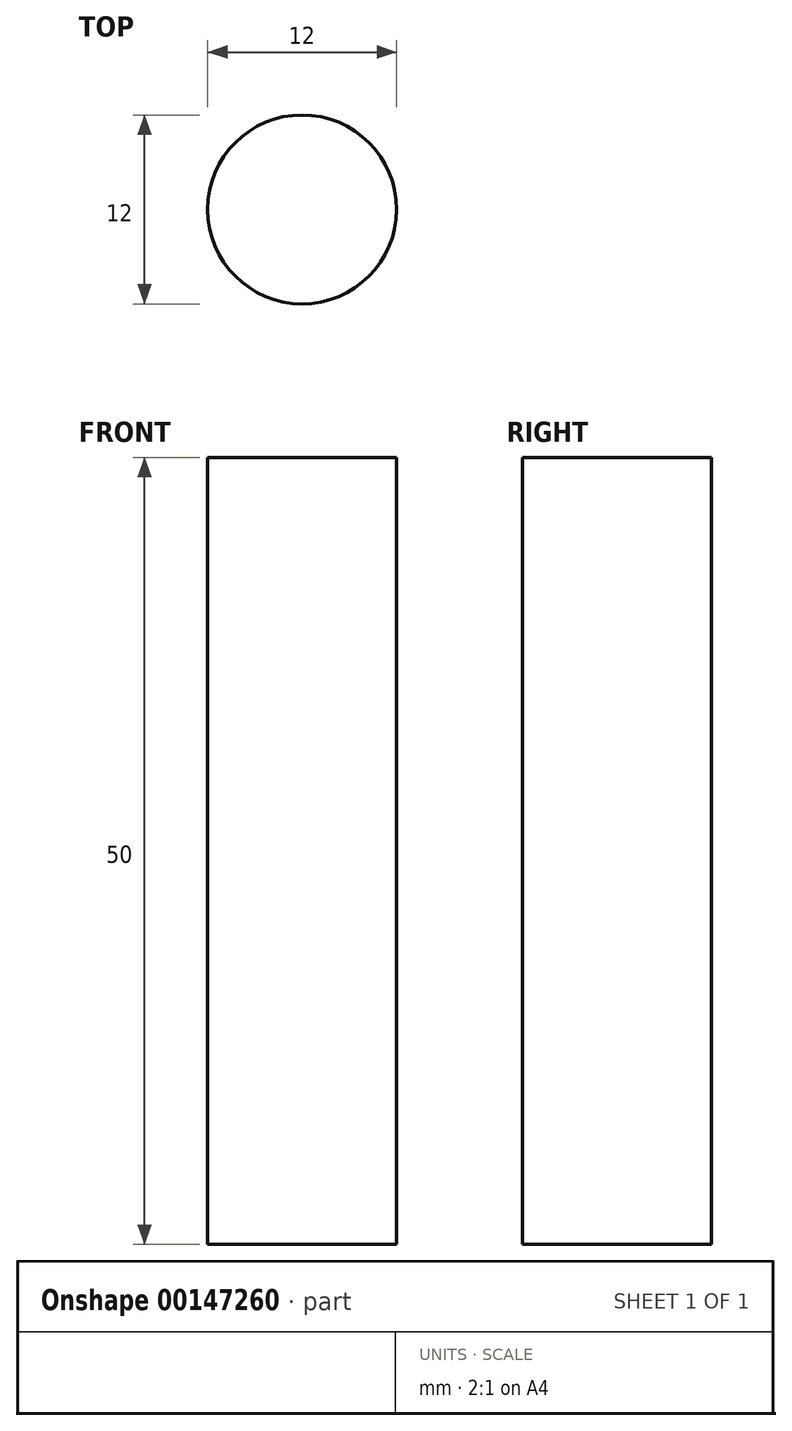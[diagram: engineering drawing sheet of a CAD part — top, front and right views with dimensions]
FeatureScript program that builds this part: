
annotation { "Feature Type Name" : "Feature", "Feature Type Description" : "" }
export const myFeature = defineFeature(function(context is Context, id is Id, definition is map)
    precondition{}
    {
        {
            var Q0;
            Q0=qCreatedBy(makeId("Top.planeOp"),FACE);
            var sketch = newSketch(context, id + "F0", { "sketchPlane" : qUnion([Q0])});
            skCircle(sketch, "E0", {"center": v(0, 0) * mm, "radius": 6 * mm});
            skSolve(sketch);
        }
        {
            var Q0;
            Q0 = qSketchRegion(id + "F0", true);
            extrude(context, id + "F1", {"entities" : qUnion([Q0]), "endBound" : BoundingType.SYMMETRIC, "depth" : 50 * mm});
        }
    });
